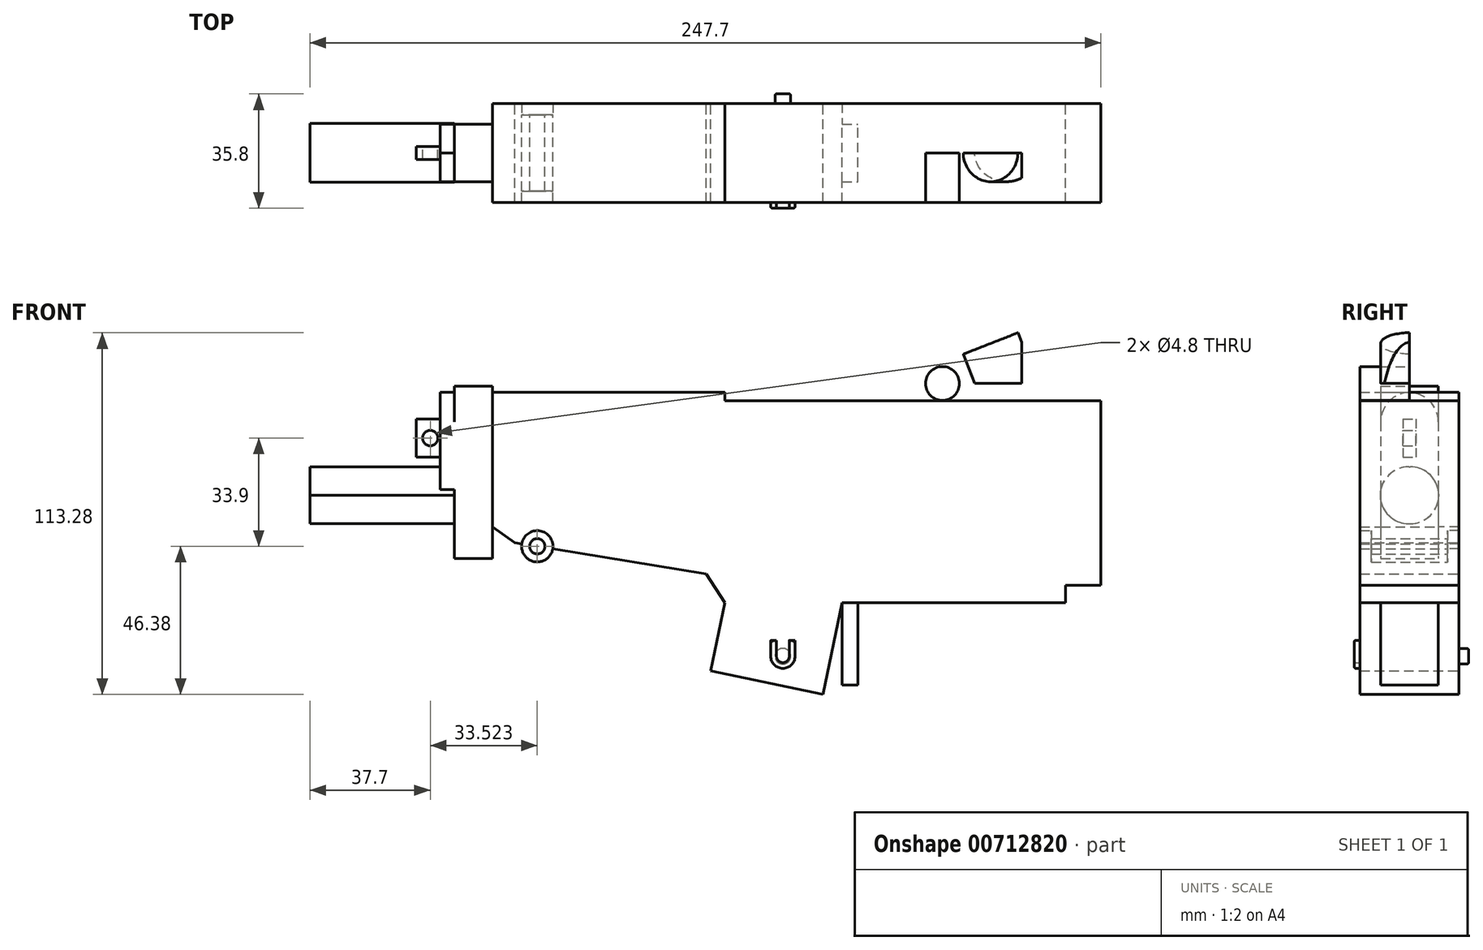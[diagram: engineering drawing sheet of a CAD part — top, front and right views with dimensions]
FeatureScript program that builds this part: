
annotation { "Feature Type Name" : "Feature", "Feature Type Description" : "" }
export const myFeature = defineFeature(function(context is Context, id is Id, definition is map)
    precondition{}
    {
        {
            var Q0;
            Q0=qCreatedBy(makeId("Front.planeOp"),FACE);
            var sketch = newSketch(context, id + "F0", { "sketchPlane" : qUnion([Q0])});
            skLineSegment(sketch, "E0.bottom", {"start": v(0, 31.65) * mm, "end": v(106.7, 31.65) * mm});
            skLineSegment(sketch, "E0.top", {"start": v(0, -31.65) * mm, "end": v(106.7, -31.65) * mm});
            skLineSegment(sketch, "E0.left", {"start": v(0, 31.65) * mm, "end": v(0, -31.65) * mm});
            skLineSegment(sketch, "E0.right", {"start": v(106.7, 31.65) * mm, "end": v(106.7, -31.65) * mm});
            skLineSegment(sketch, "E1.bottom", {"start": v(106.7, 31.65) * mm, "end": v(117.7, 31.65) * mm});
            skLineSegment(sketch, "E1.top", {"start": v(106.7, -26.15) * mm, "end": v(117.7, -26.15) * mm});
            skLineSegment(sketch, "E1.left", {"start": v(106.7, 31.65) * mm, "end": v(106.7, -26.15) * mm});
            skLineSegment(sketch, "E1.right", {"start": v(117.7, 31.65) * mm, "end": v(117.7, -26.15) * mm});
            skLineSegment(sketch, "E2.bottom", {"start": v(100.8, 31.65) * mm, "end": v(60.9, 31.65) * mm});
            skLineSegment(sketch, "E2.top", {"start": v(100.8, 37.05) * mm, "end": v(60.9, 37.05) * mm});
            skLineSegment(sketch, "E2.left", {"start": v(100.8, 31.65) * mm, "end": v(100.8, 37.05) * mm});
            skLineSegment(sketch, "E2.right", {"start": v(60.9, 31.65) * mm, "end": v(60.9, 37.05) * mm});
            skLineSegment(sketch, "E3", {"start": v(0, -31.65) * mm, "end": v(-4.46, -52.99) * mm});
            skLineSegment(sketch, "E4", {"start": v(-4.46, -52.99) * mm, "end": v(30.68, -60.33) * mm});
            skLineSegment(sketch, "E5", {"start": v(0, -31.65) * mm, "end": v(-5.88, -22.59) * mm});
            skLineSegment(sketch, "E6", {"start": v(-5.88, -22.59) * mm, "end": v(-65.88, -12.79) * mm});
            skLineSegment(sketch, "E7", {"start": v(-65.88, -12.79) * mm, "end": v(-72.8, -7.85) * mm});
            skLineSegment(sketch, "E8", {"start": v(-72.8, -7.85) * mm, "end": v(-72.8, 34.25) * mm});
            skLineSegment(sketch, "E9", {"start": v(-72.8, 34.25) * mm, "end": v(0, 34.25) * mm});
            skLineSegment(sketch, "E10", {"start": v(0, 34.25) * mm, "end": v(0, 31.65) * mm});
            skCircle(sketch, "E11", {"center": v(-58.78, -13.95) * mm, "radius": 4.9 * mm});
            skCircle(sketch, "E12", {"center": v(-58.78, -13.95) * mm, "radius": 2.4 * mm});
            skLineSegment(sketch, "E13.bottom", {"start": v(-72.8, 36.25) * mm, "end": v(-84.8, 36.25) * mm});
            skLineSegment(sketch, "E13.top", {"start": v(-72.8, -17.79) * mm, "end": v(-84.8, -17.79) * mm});
            skLineSegment(sketch, "E13.left", {"start": v(-72.8, 36.25) * mm, "end": v(-72.8, -17.79) * mm});
            skLineSegment(sketch, "E13.right", {"start": v(-84.8, 36.25) * mm, "end": v(-84.8, -17.79) * mm});
            skLineSegment(sketch, "E14.bottom", {"start": v(-84.8, 10.95) * mm, "end": v(-130, 10.95) * mm});
            skLineSegment(sketch, "E14.top", {"start": v(-84.8, -6.85) * mm, "end": v(-130, -6.85) * mm});
            skLineSegment(sketch, "E14.left", {"start": v(-84.8, 10.95) * mm, "end": v(-84.8, -6.85) * mm});
            skLineSegment(sketch, "E14.right", {"start": v(-130, 10.95) * mm, "end": v(-130, -6.85) * mm});
            skLineSegment(sketch, "E15.bottom", {"start": v(-84.8, 34.25) * mm, "end": v(-89.2, 34.25) * mm});
            skLineSegment(sketch, "E15.top", {"start": v(-84.8, 10.95) * mm, "end": v(-89.2, 10.95) * mm});
            skLineSegment(sketch, "E15.left", {"start": v(-84.8, 34.25) * mm, "end": v(-84.8, 10.95) * mm});
            skLineSegment(sketch, "E15.right", {"start": v(-89.2, 34.25) * mm, "end": v(-89.2, 10.95) * mm});
            skLineSegment(sketch, "E16.bottom", {"start": v(-89.2, 25.95) * mm, "end": v(-96.7, 25.95) * mm});
            skLineSegment(sketch, "E16.top", {"start": v(-89.2, 13.95) * mm, "end": v(-96.7, 13.95) * mm});
            skLineSegment(sketch, "E16.left", {"start": v(-89.2, 25.95) * mm, "end": v(-89.2, 13.95) * mm});
            skLineSegment(sketch, "E16.right", {"start": v(-96.7, 25.95) * mm, "end": v(-96.7, 13.95) * mm});
            skCircle(sketch, "E17", {"center": v(-92.3, 19.95) * mm, "radius": 2.4 * mm});
            skLineSegment(sketch, "E18", {"start": v(30.68, -60.33) * mm, "end": v(36.68, -31.65) * mm});
            skLineSegment(sketch, "E19", {"start": v(36.68, -31.65) * mm, "end": v(36.68, -57.45) * mm});
            skLineSegment(sketch, "E20", {"start": v(36.68, -57.45) * mm, "end": v(41.68, -57.45) * mm});
            skLineSegment(sketch, "E21", {"start": v(41.68, -57.45) * mm, "end": v(41.68, -31.65) * mm});
            skCircle(sketch, "E22", {"center": v(68.1, 37.05) * mm, "radius": 5.3 * mm});
            skLineSegment(sketch, "E23", {"start": v(74.6, 46.25) * mm, "end": v(91.74, 52.95) * mm});
            skLineSegment(sketch, "E24", {"start": v(91.74, 52.95) * mm, "end": v(92.9, 49.97) * mm});
            skLineSegment(sketch, "E25", {"start": v(92.9, 49.97) * mm, "end": v(92.9, 37.05) * mm});
            skLineSegment(sketch, "E26", {"start": v(68.1, 37.05) * mm, "end": v(68.1, 42.35) * mm});
            skLineSegment(sketch, "E27", {"start": v(74.6, 46.25) * mm, "end": v(78.2, 37.05) * mm});
            skPoint(sketch, "E28", {"position": v(-58.78, -18.85) * mm});
            skPoint(sketch, "E29", {"position": v(-130, 2.05) * mm});
            skSolve(sketch);
        }
        {
            var Q0;
            {var subQ0=sQuery(id+"F0.wireOp",EDGE,"E3");Q0=makeQuery(id+"F0.imprint","IMPRINT",FACE,{"disambiguationData":[TD([[makeQuery(id+"F0.imprint","IMPRINT",EDGE,{"derivedFrom":subQ0}),1.0]])]});}
            var Q1;
            Q1=makeQuery(id+"F0.imprint","IMPRINT",FACE,{"disambiguationData":[TD([[makeQuery(id+"F0.imprint","IMPRINT",EDGE,{"derivedFrom":sQuery(id+"F0.wireOp",EDGE,"E0.left")}),-1.0]])]});
            var Q2;
            {var subQ3=sQuery(id+"F0.wireOp",EDGE,"E0.left");Q2=makeQuery(id+"F0.imprint","IMPRINT",FACE,{"disambiguationData":[TD([[makeQuery(id+"F0.imprint","IMPRINT",EDGE,{"derivedFrom":subQ3}),1.0]])]});}
            var Q3;
            Q3=makeQuery(id+"F0.imprint","IMPRINT",FACE,{"disambiguationData":[TD([[makeQuery(id+"F0.imprint","IMPRINT",EDGE,{"derivedFrom":sQuery(id+"F0.wireOp",EDGE,"E1.bottom")}),-1.0]])]});
            var Q4;
            Q4=makeQuery(id+"F0.imprint","IMPRINT",FACE,{"disambiguationData":[TD([[makeQuery(id+"F0.imprint","IMPRINT",EDGE,{"derivedFrom":sQuery(id+"F0.wireOp",EDGE,"E2.bottom")}),-1.0]])]});
            var Q5;
            {var subQ0=sQuery(id+"F0.wireOp",EDGE,"E26");Q5=makeQuery(id+"F0.imprint","IMPRINT",FACE,{"disambiguationData":[TD([[makeQuery(id+"F0.imprint","IMPRINT",EDGE,{"derivedFrom":subQ0}),-1.0]])]});}
            var Q6;
            {var subQ0=sQuery(id+"F0.wireOp",EDGE,"E26");Q6=makeQuery(id+"F0.imprint","IMPRINT",FACE,{"disambiguationData":[TD([[makeQuery(id+"F0.imprint","IMPRINT",EDGE,{"derivedFrom":subQ0}),1.0]])]});}
            var Q7;
            {var subQ0=sQuery(id+"F0.wireOp",EDGE,"E2.top");var subQ1=makeQuery(id+"F0.imprint","INTERSECT",VERTEX,{"derivedFrom":[subQ0,sQuery(id+"F0.wireOp",EDGE,"E26")]});Q7=makeQuery(id+"F0.imprint","IMPRINT",FACE,{"disambiguationData":[TD([[makeQuery(id+"F0.imprint","IMPRINT",EDGE,{"disambiguationData":[TD([[subQ1,1.0]])],"derivedFrom":subQ0}),1.0]])]});}
            extrude(context, id + "F1", {"entities" : qUnion([Q0, Q1, Q2, Q3, Q4, Q5, Q6, Q7]), "depth" : 15.5 * mm, "offsetDistance" : 25 * mm});
        }
        {
            var Q0;
            Q0=makeQuery(id+"F0.imprint","IMPRINT",FACE,{"disambiguationData":[TD([[makeQuery(id+"F0.imprint","IMPRINT",EDGE,{"derivedFrom":sQuery(id+"F0.wireOp",EDGE,"E14.bottom")}),1.0]])]});
            extrude(context, id + "F2", {"entities" : qUnion([Q0]), "operationType" : NewBodyOperationType.ADD, "depth" : 9.2 * mm, "offsetDistance" : 25 * mm});
        }
        {
            var Q0;
            {var subQ3=sQuery(id+"F0.wireOp",EDGE,"E13.bottom");Q0=makeQuery(id+"F0.imprint","IMPRINT",FACE,{"disambiguationData":[TD([[makeQuery(id+"F0.imprint","IMPRINT",EDGE,{"derivedFrom":subQ3}),1.0]])]});}
            var Q1;
            {var subQ1=sQuery(id+"F0.wireOp",EDGE,"E15.bottom");Q1=makeQuery(id+"F0.imprint","IMPRINT",FACE,{"disambiguationData":[TD([[makeQuery(id+"F0.imprint","IMPRINT",EDGE,{"derivedFrom":subQ1}),1.0]])]});}
            var Q2;
            Q2=makeQuery(id+"F0.imprint","IMPRINT",FACE,{"disambiguationData":[TD([[makeQuery(id+"F0.imprint","IMPRINT",EDGE,{"derivedFrom":sQuery(id+"F0.wireOp",EDGE,"E23")}),-1.0]])]});
            extrude(context, id + "F3", {"entities" : qUnion([Q0, Q1, Q2]), "operationType" : NewBodyOperationType.ADD, "depth" : 9 * mm, "offsetDistance" : 25 * mm});
        }
        {
            var Q0;
            Q0=makeQuery(id+"F0.imprint","IMPRINT",FACE,{"disambiguationData":[TD([[makeQuery(id+"F0.imprint","IMPRINT",EDGE,{"derivedFrom":sQuery(id+"F0.wireOp",EDGE,"E16.bottom")}),1.0]])]});
            extrude(context, id + "F4", {"entities" : qUnion([Q0]), "operationType" : NewBodyOperationType.ADD, "depth" : 2 * mm, "offsetDistance" : 25 * mm});
        }
        {
            var Q0;
            {var subQ0=sQuery(id+"F0.wireOp",EDGE,"E19");Q0=makeQuery(id+"F0.imprint","IMPRINT",FACE,{"disambiguationData":[TD([[makeQuery(id+"F0.imprint","IMPRINT",EDGE,{"derivedFrom":subQ0}),1.0]])]});}
            extrude(context, id + "F5", {"entities" : qUnion([Q0]), "operationType" : NewBodyOperationType.ADD, "depth" : 9 * mm, "offsetDistance" : 25 * mm});
        }
        {
            var Q0;
            {var subQ0=sQuery(id+"F0.wireOp",EDGE,"E11");var subQ1=sQuery(id+"F0.wireOp",EDGE,"E6");var subQ2=makeQuery(id+"F0.imprint","INTERSECT",VERTEX,{"disambiguationData":[OD(0.0)],"derivedFrom":[subQ1,subQ0]});Q0=makeQuery(id+"F0.imprint","IMPRINT",FACE,{"disambiguationData":[TD([[makeQuery(id+"F0.imprint","IMPRINT",EDGE,{"disambiguationData":[TD([[subQ2,-1.0]])],"derivedFrom":subQ1}),1.0]])]});}
            var Q1;
            {var subQ0=sQuery(id+"F0.wireOp",EDGE,"E11");var subQ1=sQuery(id+"F0.wireOp",EDGE,"E6");var subQ2=makeQuery(id+"F0.imprint","INTERSECT",VERTEX,{"disambiguationData":[OD(0.0)],"derivedFrom":[subQ1,subQ0]});Q1=makeQuery(id+"F0.imprint","IMPRINT",FACE,{"disambiguationData":[TD([[makeQuery(id+"F0.imprint","IMPRINT",EDGE,{"disambiguationData":[TD([[subQ2,-1.0]])],"derivedFrom":subQ1}),-1.0]])]});}
            extrude(context, id + "F6", {"entities" : qUnion([Q0, Q1]), "operationType" : NewBodyOperationType.ADD, "depth" : 11.95 * mm, "offsetDistance" : 25 * mm});
        }
        {
            var Q0;
            Q0=makeQuery(id+"F3.opExtrude","CAP_EDGE",EDGE,{"disambiguationData":[OSD([sQuery(id+"F0.wireOp",EDGE,"E27")])],"isStart":false});
            var Q1;
            Q1=makeQuery(id+"F3.opExtrude","CAP_EDGE",EDGE,{"disambiguationData":[OSD([sQuery(id+"F0.wireOp",EDGE,"E24")])],"isStart":false});
            fillet(context, id + "F7", {"entities" : qUnion([Q0, Q1]), "radius" : 9.2 * mm, "tangentPropagation" : true, "allowEdgeOverflow" : false});
        }
        {
            var Q0;
            Q0=makeQuery(id+"F3.opExtrude","CAP_EDGE",EDGE,{"disambiguationData":[OSD([sQuery(id+"F0.wireOp",EDGE,"E15.top")])],"isStart":false});
            var Q1;
            Q1=makeQuery(id+"F3.opExtrude","CAP_EDGE",EDGE,{"disambiguationData":[OSD([sQuery(id+"F0.wireOp",EDGE,"E15.bottom")])],"isStart":false});
            fillet(context, id + "F8", {"entities" : qUnion([Q0, Q1]), "radius" : 9.2 * mm, "tangentPropagation" : true, "allowEdgeOverflow" : false});
        }
        {
            var Q0;
            Q0=makeQuery(id+"F2.opExtrude","CAP_EDGE",EDGE,{"disambiguationData":[OSD([sQuery(id+"F0.wireOp",EDGE,"E14.top")])],"isStart":false});
            var Q1;
            Q1=makeQuery(id+"F2.opExtrude","CAP_EDGE",EDGE,{"disambiguationData":[OSD([sQuery(id+"F0.wireOp",EDGE,"E14.bottom"),sQuery(id+"F0.wireOp",EDGE,"E15.top")])],"isStart":false});
            fillet(context, id + "F9", {"entities" : qUnion([Q0, Q1]), "radius" : 9 * mm, "tangentPropagation" : true, "allowEdgeOverflow" : false});
        }
        {
            var Q0;
            Q0=makeQuery(id+"F1.opExtrude","SWEPT_BODY",BODY,{"disambiguationData":[OSD([sQuery(id+"F0.wireOp",EDGE,"E0.bottom"),sQuery(id+"F0.wireOp",EDGE,"E0.top"),sQuery(id+"F0.wireOp",EDGE,"E0.right"),sQuery(id+"F0.wireOp",EDGE,"E1.bottom"),sQuery(id+"F0.wireOp",EDGE,"E1.top"),sQuery(id+"F0.wireOp",EDGE,"E1.right"),sQuery(id+"F0.wireOp",EDGE,"E2.top"),sQuery(id+"F0.wireOp",EDGE,"E2.left"),sQuery(id+"F0.wireOp",EDGE,"E2.right"),sQuery(id+"F0.wireOp",EDGE,"E3"),sQuery(id+"F0.wireOp",EDGE,"E4"),sQuery(id+"F0.wireOp",EDGE,"E5"),sQuery(id+"F0.wireOp",EDGE,"E6"),sQuery(id+"F0.wireOp",EDGE,"E7"),sQuery(id+"F0.wireOp",EDGE,"E9"),sQuery(id+"F0.wireOp",EDGE,"E10"),sQuery(id+"F0.wireOp",EDGE,"E11"),sQuery(id+"F0.wireOp",EDGE,"E13.left"),sQuery(id+"F0.wireOp",EDGE,"E18"),sQuery(id+"F0.wireOp",EDGE,"E22")])]});
            var Q1;
            Q1=qCreatedBy(makeId("Front.planeOp"),FACE);
            mirror(context, id + "F10", {"operationType" : NewBodyOperationType.ADD, "entities" : qUnion([Q0]), "mirrorPlane" : qUnion([Q1])});
        }
        {
            var Q0;
            Q0=makeQuery(id+"F1.opExtrude","CAP_FACE",FACE,{"disambiguationData":[OSD([sQuery(id+"F0.wireOp",EDGE,"E0.bottom"),sQuery(id+"F0.wireOp",EDGE,"E0.top"),sQuery(id+"F0.wireOp",EDGE,"E0.right"),sQuery(id+"F0.wireOp",EDGE,"E1.bottom"),sQuery(id+"F0.wireOp",EDGE,"E1.top"),sQuery(id+"F0.wireOp",EDGE,"E1.right"),sQuery(id+"F0.wireOp",EDGE,"E2.top"),sQuery(id+"F0.wireOp",EDGE,"E2.left"),sQuery(id+"F0.wireOp",EDGE,"E2.right"),sQuery(id+"F0.wireOp",EDGE,"E3"),sQuery(id+"F0.wireOp",EDGE,"E4"),sQuery(id+"F0.wireOp",EDGE,"E5"),sQuery(id+"F0.wireOp",EDGE,"E6"),sQuery(id+"F0.wireOp",EDGE,"E7"),sQuery(id+"F0.wireOp",EDGE,"E9"),sQuery(id+"F0.wireOp",EDGE,"E10"),sQuery(id+"F0.wireOp",EDGE,"E11"),sQuery(id+"F0.wireOp",EDGE,"E13.left"),sQuery(id+"F0.wireOp",EDGE,"E18"),sQuery(id+"F0.wireOp",EDGE,"E22")])],"isStart":false});
            var sketch = newSketch(context, id + "F11", { "sketchPlane" : qUnion([Q0])});
            skCircle(sketch, "E30", {"center": v(-58.78, -13.95) * mm, "radius": 2 * mm});
            skCircle(sketch, "E31", {"center": v(18.12, -48.37) * mm, "radius": 2.45 * mm});
            skCircle(sketch, "E32", {"center": v(18.12, -48.37) * mm, "radius": 2 * mm});
            skCircle(sketch, "E33", {"center": v(18.12, -48.37) * mm, "radius": 3.8 * mm});
            skLineSegment(sketch, "E34", {"start": v(14.32, -48.37) * mm, "end": v(14.32, -43.37) * mm});
            skLineSegment(sketch, "E35", {"start": v(16.12, -48.37) * mm, "end": v(16.12, -43.37) * mm});
            skPoint(sketch, "E36", {"position": v(18.12, -52.17) * mm});
            skLineSegment(sketch, "E37", {"start": v(14.32, -43.37) * mm, "end": v(16.12, -43.37) * mm});
            skLineSegment(sketch, "E38", {"start": v(18.12, -48.37) * mm, "end": v(18.12, -52.17) * mm});
            skLineSegment(sketch, "E39.MirrorCS", {"start": v(21.92, -48.37) * mm, "end": v(21.92, -43.37) * mm});
            skLineSegment(sketch, "E40.MirrorCS", {"start": v(21.92, -43.37) * mm, "end": v(20.12, -43.37) * mm});
            skLineSegment(sketch, "E41.MirrorCS", {"start": v(20.12, -48.37) * mm, "end": v(20.12, -43.37) * mm});
            skSolve(sketch);
        }
        {
            var Q0;
            {var subQ0=sQuery(id+"F11.wireOp",EDGE,"E34");Q0=makeQuery(id+"F11.imprint","IMPRINT",FACE,{"disambiguationData":[TD([[makeQuery(id+"F11.imprint","IMPRINT",EDGE,{"derivedFrom":subQ0}),-1.0]])]});}
            var Q1;
            {var subQ4=sQuery(id+"F11.wireOp",EDGE,"E35");var subQ5=sQuery(id+"F11.wireOp",EDGE,"E31");var subQ6=makeQuery(id+"F11.imprint","INTERSECT",VERTEX,{"derivedFrom":[subQ5,subQ4]});Q1=makeQuery(id+"F11.imprint","IMPRINT",FACE,{"disambiguationData":[TD([[makeQuery(id+"F11.imprint","IMPRINT",EDGE,{"disambiguationData":[TD([[subQ6,-1.0]])],"derivedFrom":subQ5}),-1.0]])]});}
            var Q2;
            {var subQ0=sQuery(id+"F11.wireOp",EDGE,"E35");var subQ1=sQuery(id+"F11.wireOp",EDGE,"E31");var subQ2=makeQuery(id+"F11.imprint","INTERSECT",VERTEX,{"derivedFrom":[subQ1,subQ0]});Q2=makeQuery(id+"F11.imprint","IMPRINT",FACE,{"disambiguationData":[TD([[makeQuery(id+"F11.imprint","IMPRINT",EDGE,{"disambiguationData":[TD([[subQ2,-1.0]])],"derivedFrom":subQ1}),1.0]])]});}
            var Q3;
            {var subQ0=sQuery(id+"F11.wireOp",EDGE,"E41.MirrorCS");var subQ1=sQuery(id+"F11.wireOp",EDGE,"E31");var subQ2=makeQuery(id+"F11.imprint","INTERSECT",VERTEX,{"derivedFrom":[subQ1,subQ0]});Q3=makeQuery(id+"F11.imprint","IMPRINT",FACE,{"disambiguationData":[TD([[makeQuery(id+"F11.imprint","IMPRINT",EDGE,{"disambiguationData":[TD([[subQ2,1.0]])],"derivedFrom":subQ1}),1.0]])]});}
            var Q4;
            {var subQ4=sQuery(id+"F11.wireOp",EDGE,"E41.MirrorCS");var subQ5=sQuery(id+"F11.wireOp",EDGE,"E31");var subQ6=makeQuery(id+"F11.imprint","INTERSECT",VERTEX,{"derivedFrom":[subQ5,subQ4]});Q4=makeQuery(id+"F11.imprint","IMPRINT",FACE,{"disambiguationData":[TD([[makeQuery(id+"F11.imprint","IMPRINT",EDGE,{"disambiguationData":[TD([[subQ6,1.0]])],"derivedFrom":subQ5}),-1.0]])]});}
            var Q5;
            {var subQ0=sQuery(id+"F11.wireOp",EDGE,"E39.MirrorCS");Q5=makeQuery(id+"F11.imprint","IMPRINT",FACE,{"disambiguationData":[TD([[makeQuery(id+"F11.imprint","IMPRINT",EDGE,{"derivedFrom":subQ0}),1.0]])]});}
            extrude(context, id + "F12", {"entities" : qUnion([Q0, Q1, Q2, Q3, Q4, Q5]), "operationType" : NewBodyOperationType.ADD, "depth" : 1.8 * mm, "offsetDistance" : 25 * mm});
        }
        {
            var Q0;
            {var subQ0=sQuery(id+"F11.wireOp",EDGE,"E35");var subQ1=sQuery(id+"F11.wireOp",EDGE,"E31");var subQ2=makeQuery(id+"F11.imprint","INTERSECT",VERTEX,{"derivedFrom":[subQ1,subQ0]});Q0=makeQuery(id+"F11.imprint","IMPRINT",FACE,{"disambiguationData":[TD([[makeQuery(id+"F11.imprint","IMPRINT",EDGE,{"disambiguationData":[TD([[subQ2,-1.0]])],"derivedFrom":subQ1}),1.0]])]});}
            var Q1;
            {var subQ0=sQuery(id+"F11.wireOp",EDGE,"E35");var subQ1=sQuery(id+"F11.wireOp",EDGE,"E31");var subQ2=makeQuery(id+"F11.imprint","INTERSECT",VERTEX,{"derivedFrom":[subQ1,subQ0]});Q1=makeQuery(id+"F11.imprint","IMPRINT",FACE,{"disambiguationData":[TD([[makeQuery(id+"F11.imprint","IMPRINT",EDGE,{"disambiguationData":[TD([[subQ2,1.0]])],"derivedFrom":subQ1}),1.0]])]});}
            var Q2;
            {var subQ0=sQuery(id+"F11.wireOp",EDGE,"E41.MirrorCS");var subQ1=sQuery(id+"F11.wireOp",EDGE,"E31");var subQ2=makeQuery(id+"F11.imprint","INTERSECT",VERTEX,{"derivedFrom":[subQ1,subQ0]});Q2=makeQuery(id+"F11.imprint","IMPRINT",FACE,{"disambiguationData":[TD([[makeQuery(id+"F11.imprint","IMPRINT",EDGE,{"disambiguationData":[TD([[subQ2,1.0]])],"derivedFrom":subQ1}),1.0]])]});}
            var Q3;
            {var subQ0=sQuery(id+"F11.wireOp",EDGE,"E32");var subQ1=makeQuery(id+"F11.imprint","INTERSECT",VERTEX,{"derivedFrom":[subQ0,sQuery(id+"F11.wireOp",EDGE,"E35")]});Q3=makeQuery(id+"F11.imprint","IMPRINT",FACE,{"disambiguationData":[TD([[makeQuery(id+"F11.imprint","IMPRINT",EDGE,{"disambiguationData":[TD([[subQ1,1.0]])],"derivedFrom":subQ0}),1.0]])]});}
            extrude(context, id + "F13", {"entities" : qUnion([Q0, Q1, Q2, Q3]), "operationType" : NewBodyOperationType.ADD, "oppositeDirection" : true, "depth" : 34 * mm, "offsetDistance" : 25 * mm});
        }
        {
            var Q0;
            Q0=makeQuery(id+"F13.opExtrude","CAP_EDGE",EDGE,{"disambiguationData":[OSD([sQuery(id+"F11.wireOp",EDGE,"E31")])],"isStart":false});
            fillet(context, id + "F14", {"entities" : qUnion([Q0]), "radius" : 0.5 * mm, "tangentPropagation" : true, "allowEdgeOverflow" : false});
        }
        {
            var Q0;
            Q0=makeQuery(id+"F12.opExtrude","CAP_EDGE",EDGE,{"disambiguationData":[OSD([sQuery(id+"F11.wireOp",EDGE,"E34")])],"isStart":false});
            var Q1;
            Q1=makeQuery(id+"F12.opExtrude","CAP_EDGE",EDGE,{"disambiguationData":[OSD([sQuery(id+"F11.wireOp",EDGE,"E33")])],"isStart":false});
            var Q2;
            Q2=makeQuery(id+"F12.opExtrude","CAP_EDGE",EDGE,{"disambiguationData":[OSD([sQuery(id+"F11.wireOp",EDGE,"E35")])],"isStart":false});
            var Q3;
            Q3=makeQuery(id+"F12.opExtrude","CAP_EDGE",EDGE,{"disambiguationData":[OSD([sQuery(id+"F11.wireOp",EDGE,"E40.MirrorCS")])],"isStart":false});
            var Q4;
            Q4=makeQuery(id+"F12.opExtrude","CAP_EDGE",EDGE,{"disambiguationData":[OSD([sQuery(id+"F11.wireOp",EDGE,"E37")])],"isStart":false});
            fillet(context, id + "F15", {"entities" : qUnion([Q0, Q1, Q2, Q3, Q4]), "radius" : 0.5 * mm, "tangentPropagation" : true, "allowEdgeOverflow" : false});
        }
    });
